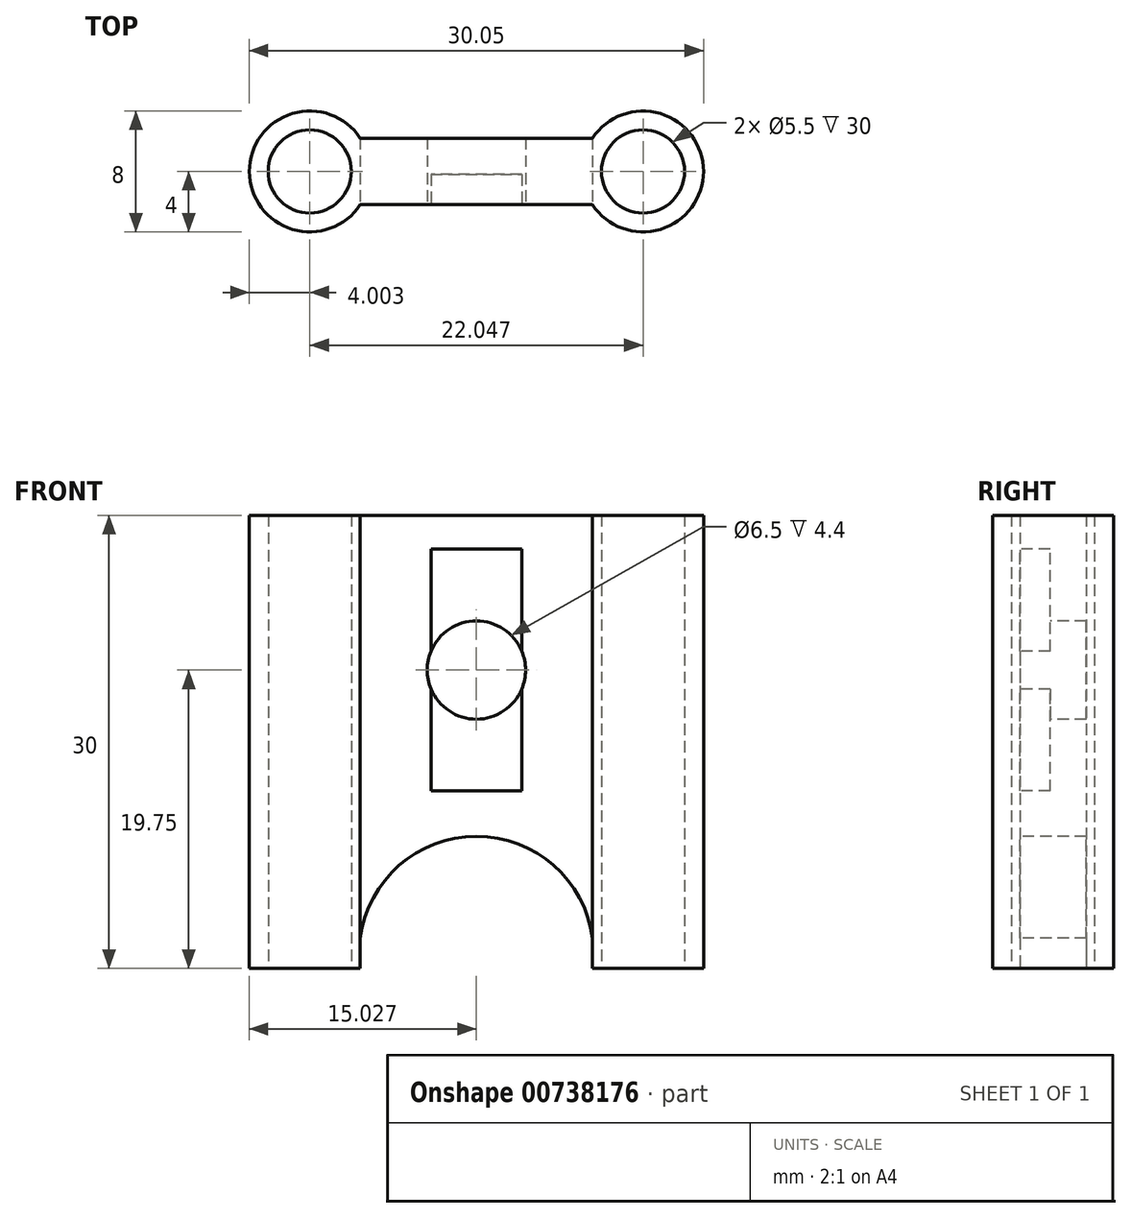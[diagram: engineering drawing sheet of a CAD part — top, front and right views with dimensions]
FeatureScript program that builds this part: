
annotation { "Feature Type Name" : "Feature", "Feature Type Description" : "" }
export const myFeature = defineFeature(function(context is Context, id is Id, definition is map)
    precondition{}
    {
        {
            var Q0;
            Q0=qCreatedBy(makeId("Top.planeOp"),FACE);
            var sketch = newSketch(context, id + "F0", { "sketchPlane" : qUnion([Q0])});
            skCircle(sketch, "E0.MirrorC", {"center": v(11.2, 0) * mm, "radius": 2.75 * mm});
            skLineSegment(sketch, "E1", {"start": v(-8.6, 1.58) * mm, "end": v(8.95, 1.58) * mm});
            skCircle(sketch, "E2", {"center": v(-10.85, 0) * mm, "radius": 4 * mm});
            skCircle(sketch, "E3", {"center": v(11.2, 0) * mm, "radius": 4 * mm});
            skCircle(sketch, "E4", {"center": v(-10.85, 0) * mm, "radius": 2.75 * mm});
            skLineSegment(sketch, "E5.bottom", {"start": v(-7.5, 2.2) * mm, "end": v(7.86, 2.2) * mm});
            skLineSegment(sketch, "E5.top", {"start": v(-7.5, -2.2) * mm, "end": v(7.86, -2.2) * mm});
            skLineSegment(sketch, "E5.left", {"start": v(-7.5, 2.2) * mm, "end": v(-7.5, -2.2) * mm});
            skLineSegment(sketch, "E5.right", {"start": v(7.86, 2.2) * mm, "end": v(7.86, -2.2) * mm});
            skSolve(sketch);
        }
        {
            var Q0;
            Q0 = qSketchRegion(id + "F0", true);
            extrude(context, id + "F1", {"entities" : qUnion([Q0]), "depth" : 30 * mm, "offsetDistance" : 25 * mm});
        }
        {
            var Q0;
            Q0=makeQuery(id+"F1.opExtrude","SWEPT_FACE",FACE,{"disambiguationData":[OSD([sQuery(id+"F0.wireOp",EDGE,"E5.top")])]});
            var sketch = newSketch(context, id + "F2", { "sketchPlane" : qUnion([Q0])});
            skLineSegment(sketch, "E6", {"start": v(-7.5, 30) * mm, "end": v(7.86, 30) * mm, "construction": true});
            skPoint(sketch, "E7", {"position": v(0.18, 30) * mm});
            skCircle(sketch, "E8", {"center": v(0.18, 19.75) * mm, "radius": 3.25 * mm});
            skLineSegment(sketch, "E9.bottom", {"start": v(-2.82, 11.75) * mm, "end": v(3.18, 11.75) * mm});
            skLineSegment(sketch, "E9.top", {"start": v(-2.82, 27.75) * mm, "end": v(3.18, 27.75) * mm});
            skLineSegment(sketch, "E9.left", {"start": v(-2.82, 11.75) * mm, "end": v(-2.82, 27.75) * mm});
            skLineSegment(sketch, "E9.right", {"start": v(3.18, 11.75) * mm, "end": v(3.18, 27.75) * mm});
            skSolve(sketch);
        }
        {
            var Q0;
            {var subQ0=sQuery(id+"F2.wireOp",EDGE,"E8");var subQ1=makeQuery(id+"F2.imprint","INTERSECT",VERTEX,{"derivedFrom":[subQ0,sQuery(id+"F2.wireOp",EDGE,"tJ0ZTpVN-KNtP-6k1g-HZu1-zXQGe7A9H4EI.left")]});Q0=makeQuery(id+"F2.imprint","IMPRINT",FACE,{"disambiguationData":[TD([[makeQuery(id+"F2.imprint","IMPRINT",EDGE,{"disambiguationData":[TD([[subQ1,1.0]])],"derivedFrom":subQ0}),1.0]])]});}
            extrude(context, id + "F3", {"entities" : qUnion([Q0]), "operationType" : NewBodyOperationType.REMOVE, "endBound" : BoundingType.UP_TO_NEXT, "oppositeDirection" : true, "depth" : 25 * mm, "offsetDistance" : 25 * mm});
        }
        {
            var Q0;
            Q0 = qSketchRegion(id + "F2", true);
            extrude(context, id + "F4", {"entities" : qUnion([Q0]), "operationType" : NewBodyOperationType.REMOVE, "oppositeDirection" : true, "depth" : 2 * mm, "offsetDistance" : 25 * mm});
        }
        {
            var Q0;
            {var subQ0=sQuery(id+"F2.wireOp",EDGE,"E9.left");var subQ1=sQuery(id+"F2.wireOp",EDGE,"E8");var subQ2=makeQuery(id+"F2.imprint","INTERSECT",VERTEX,{"disambiguationData":[OD(0.0)],"derivedFrom":[subQ1,subQ0]});var subQ3=makeQuery(id+"F2.imprint","INTERSECT",VERTEX,{"disambiguationData":[OD(1.0)],"derivedFrom":[subQ1,subQ0]});var subQ4=sQuery(id+"F2.wireOp",EDGE,"E9.right");var subQ5=sQuery(id+"F2.wireOp",EDGE,"E9.top");var subQ6=sQuery(id+"F2.wireOp",EDGE,"E9.bottom");var subQ7=makeQuery(id+"F4.opExtrude","CAP_FACE",FACE,{"disambiguationData":[OSD([subQ1,subQ6,subQ5,subQ0,subQ4])],"isStart":false});Q0=makeQuery(id+"F4.boolean.opBoolean","COPY",FACE,{"disambiguationData":[TD([makeQuery(id+"F3.boolean.opBoolean","COPY",FACE,{"derivedFrom":makeQuery(id+"F3.opExtrude","SWEPT_FACE",FACE,{"disambiguationData":[OSD([subQ1]),TDD([makeQuery(id+"F2.imprint","IMPRINT",EDGE,{"disambiguationData":[TD([[subQ2,1.0]])],"derivedFrom":subQ1})])]})}),makeQuery(id+"F3.boolean.opBoolean","COPY",FACE,{"derivedFrom":makeQuery(id+"F3.opExtrude","SWEPT_FACE",FACE,{"disambiguationData":[OSD([subQ1]),TDD([makeQuery(id+"F2.imprint","IMPRINT",EDGE,{"disambiguationData":[TD([[subQ3,-1.0]])],"derivedFrom":subQ1})])]})}),makeQuery(id+"F3.boolean.opBoolean","COPY",FACE,{"derivedFrom":makeQuery(id+"F3.opExtrude","SWEPT_FACE",FACE,{"disambiguationData":[OSD([subQ0])]})}),makeQuery(id+"F4.opExtrude","SWEPT_FACE",FACE,{"disambiguationData":[OSD([subQ1]),TDD([makeQuery(id+"F2.imprint","IMPRINT",EDGE,{"disambiguationData":[TD([[subQ2,-1.0]])],"derivedFrom":subQ1})])]}),subQ7,makeQuery(id+"F4.opExtrude","SWEPT_FACE",FACE,{"disambiguationData":[OSD([subQ0]),TDD([makeQuery(id+"F2.imprint","IMPRINT",EDGE,{"disambiguationData":[TD([[makeQuery(id+"F2.imprint","INTERSECT",VERTEX,{"derivedFrom":[subQ6,subQ0]}),-1.0]])],"derivedFrom":subQ0})])]}),makeQuery(id+"F4.opExtrude","SWEPT_FACE",FACE,{"disambiguationData":[OSD([subQ0]),TDD([makeQuery(id+"F2.imprint","IMPRINT",EDGE,{"disambiguationData":[TD([[makeQuery(id+"F2.imprint","INTERSECT",VERTEX,{"derivedFrom":[subQ5,subQ0]}),1.0]])],"derivedFrom":subQ0})])]})])],"derivedFrom":subQ7});}
            var Q1;
            {var subQ0=sQuery(id+"F2.wireOp",EDGE,"E9.right");var subQ1=sQuery(id+"F2.wireOp",EDGE,"E9.left");var subQ2=sQuery(id+"F2.wireOp",EDGE,"E9.top");var subQ3=sQuery(id+"F2.wireOp",EDGE,"E9.bottom");var subQ4=sQuery(id+"F2.wireOp",EDGE,"E8");var subQ5=makeQuery(id+"F4.opExtrude","CAP_FACE",FACE,{"disambiguationData":[OSD([subQ4,subQ3,subQ2,subQ1,subQ0])],"isStart":false});var subQ7=makeQuery(id+"F2.imprint","INTERSECT",VERTEX,{"disambiguationData":[OD(0.0)],"derivedFrom":[subQ4,subQ0]});Q1=makeQuery(id+"F4.boolean.opBoolean","COPY",FACE,{"disambiguationData":[TD([makeQuery(id+"F3.boolean.opBoolean","COPY",FACE,{"derivedFrom":makeQuery(id+"F3.opExtrude","SWEPT_FACE",FACE,{"disambiguationData":[OSD([subQ4]),TDD([makeQuery(id+"F2.imprint","IMPRINT",EDGE,{"disambiguationData":[TD([[makeQuery(id+"F2.imprint","INTERSECT",VERTEX,{"disambiguationData":[OD(0.0)],"derivedFrom":[subQ4,subQ1]}),1.0]])],"derivedFrom":subQ4})])]})}),makeQuery(id+"F3.boolean.opBoolean","COPY",FACE,{"derivedFrom":makeQuery(id+"F3.opExtrude","SWEPT_FACE",FACE,{"disambiguationData":[OSD([subQ4]),TDD([makeQuery(id+"F2.imprint","IMPRINT",EDGE,{"disambiguationData":[TD([[makeQuery(id+"F2.imprint","INTERSECT",VERTEX,{"disambiguationData":[OD(1.0)],"derivedFrom":[subQ4,subQ1]}),-1.0]])],"derivedFrom":subQ4})])]})}),makeQuery(id+"F3.boolean.opBoolean","COPY",FACE,{"derivedFrom":makeQuery(id+"F3.opExtrude","SWEPT_FACE",FACE,{"disambiguationData":[OSD([subQ0])]})}),subQ5,makeQuery(id+"F4.opExtrude","SWEPT_FACE",FACE,{"disambiguationData":[OSD([subQ4]),TDD([makeQuery(id+"F2.imprint","IMPRINT",EDGE,{"disambiguationData":[TD([[subQ7,1.0]])],"derivedFrom":subQ4})])]}),makeQuery(id+"F4.opExtrude","SWEPT_FACE",FACE,{"disambiguationData":[OSD([subQ0]),TDD([makeQuery(id+"F2.imprint","IMPRINT",EDGE,{"disambiguationData":[TD([[makeQuery(id+"F2.imprint","INTERSECT",VERTEX,{"derivedFrom":[subQ3,subQ0]}),-1.0]])],"derivedFrom":subQ0})])]}),makeQuery(id+"F4.opExtrude","SWEPT_FACE",FACE,{"disambiguationData":[OSD([subQ0]),TDD([makeQuery(id+"F2.imprint","IMPRINT",EDGE,{"disambiguationData":[TD([[makeQuery(id+"F2.imprint","INTERSECT",VERTEX,{"derivedFrom":[subQ2,subQ0]}),1.0]])],"derivedFrom":subQ0})])]})])],"derivedFrom":subQ5});}
            extrude(context, id + "F5", {"entities" : qUnion([Q0, Q1]), "operationType" : NewBodyOperationType.REMOVE, "endBound" : BoundingType.UP_TO_NEXT, "oppositeDirection" : true, "depth" : 25 * mm, "offsetDistance" : 25 * mm});
        }
        {
            var Q0;
            Q0=makeQuery(id+"F1.opExtrude","SWEPT_FACE",FACE,{"disambiguationData":[OSD([sQuery(id+"F0.wireOp",EDGE,"E5.top")])]});
            var sketch = newSketch(context, id + "F6", { "sketchPlane" : qUnion([Q0])});
            skArc(sketch, "E10", {"start": v(7.86, 0) * mm, "mid": v(0.18, 8.75) * mm, "end": v(-7.5, 0) * mm});
            skSolve(sketch);
        }
        {
            var Q0;
            Q0 = qSketchRegion(id + "F6", true);
            var Q1;
            {var subQ1=sQuery(id+"F0.wireOp",EDGE,"E5.top");var subQ6=makeQuery(id+"F1.opExtrude","CAP_EDGE",EDGE,{"disambiguationData":[OSD([subQ1])],"isStart":true});Q1=makeQuery(id+"F6.imprint","IMPRINT",FACE,{"disambiguationData":[TD([[makeQuery(id+"F6.imprint","IMPRINT",EDGE,{"derivedFrom":subQ6}),1.0]])]});}
            extrude(context, id + "F7", {"entities" : qUnion([Q0, Q1]), "operationType" : NewBodyOperationType.REMOVE, "endBound" : BoundingType.UP_TO_NEXT, "oppositeDirection" : true, "depth" : 25 * mm, "offsetDistance" : 25 * mm});
        }
    });
